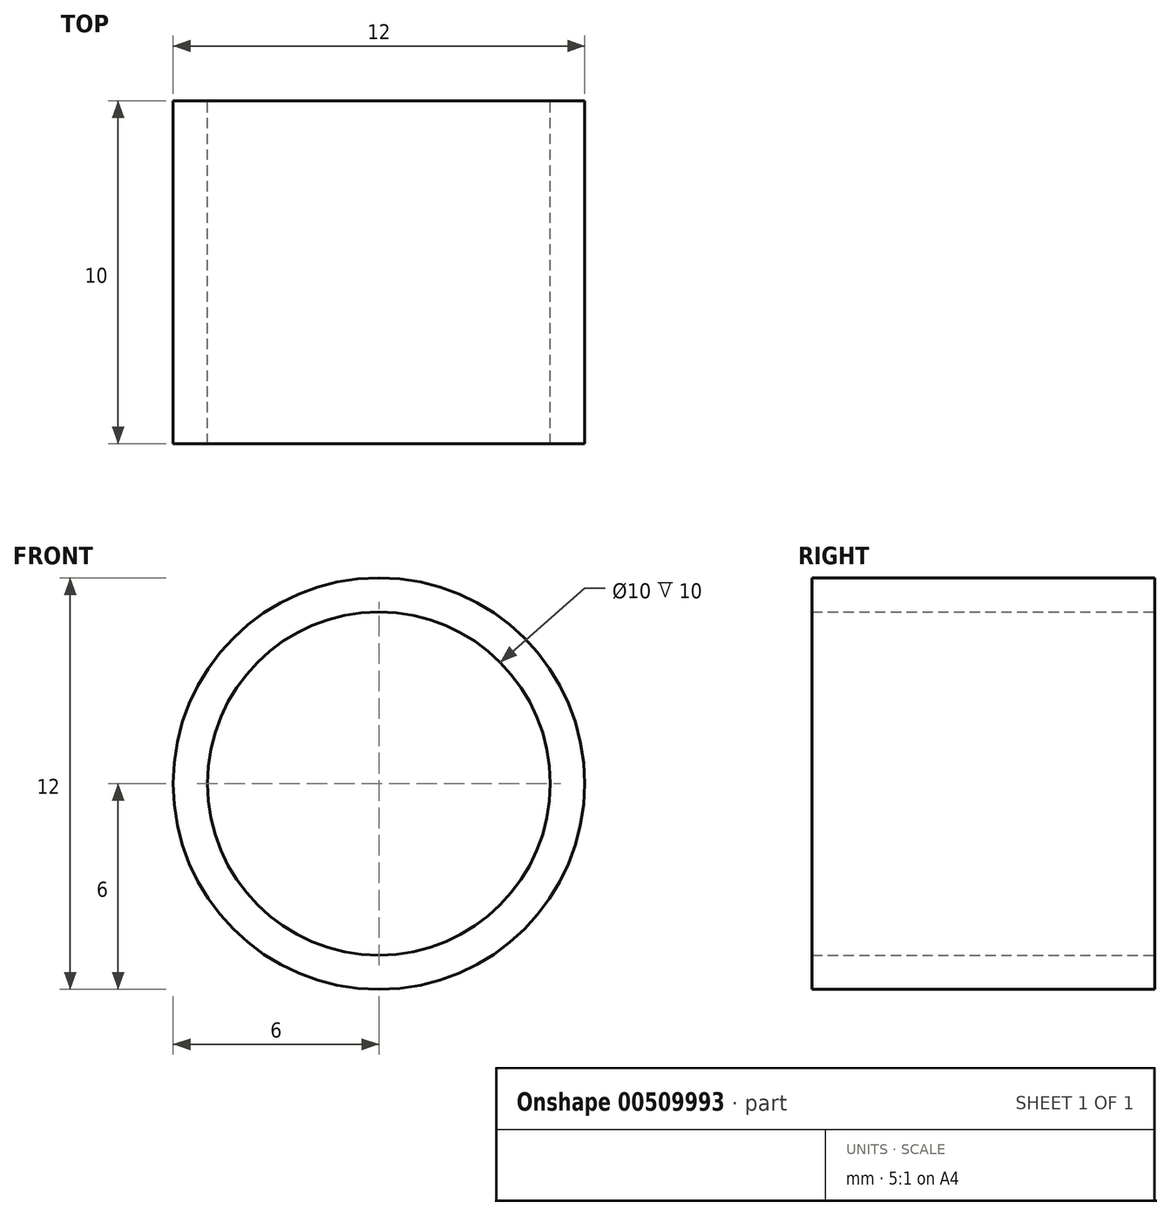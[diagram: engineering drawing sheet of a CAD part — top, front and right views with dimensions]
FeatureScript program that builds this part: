
annotation { "Feature Type Name" : "Feature", "Feature Type Description" : "" }
export const myFeature = defineFeature(function(context is Context, id is Id, definition is map)
    precondition{}
    {
        {
            var Q0;
            Q0=qCreatedBy(makeId("Front.planeOp"),FACE);
            var sketch = newSketch(context, id + "F0", { "sketchPlane" : qUnion([Q0])});
            skCircle(sketch, "E0", {"center": v(0, 0) * mm, "radius": 5 * mm});
            skCircle(sketch, "E1", {"center": v(0, 0) * mm, "radius": 6 * mm});
            skSolve(sketch);
        }
        {
            var Q0;
            Q0 = qSketchRegion(id + "F0", true);
            extrude(context, id + "F1", {"entities" : qUnion([Q0]), "depth" : 10 * mm});
        }
    });
